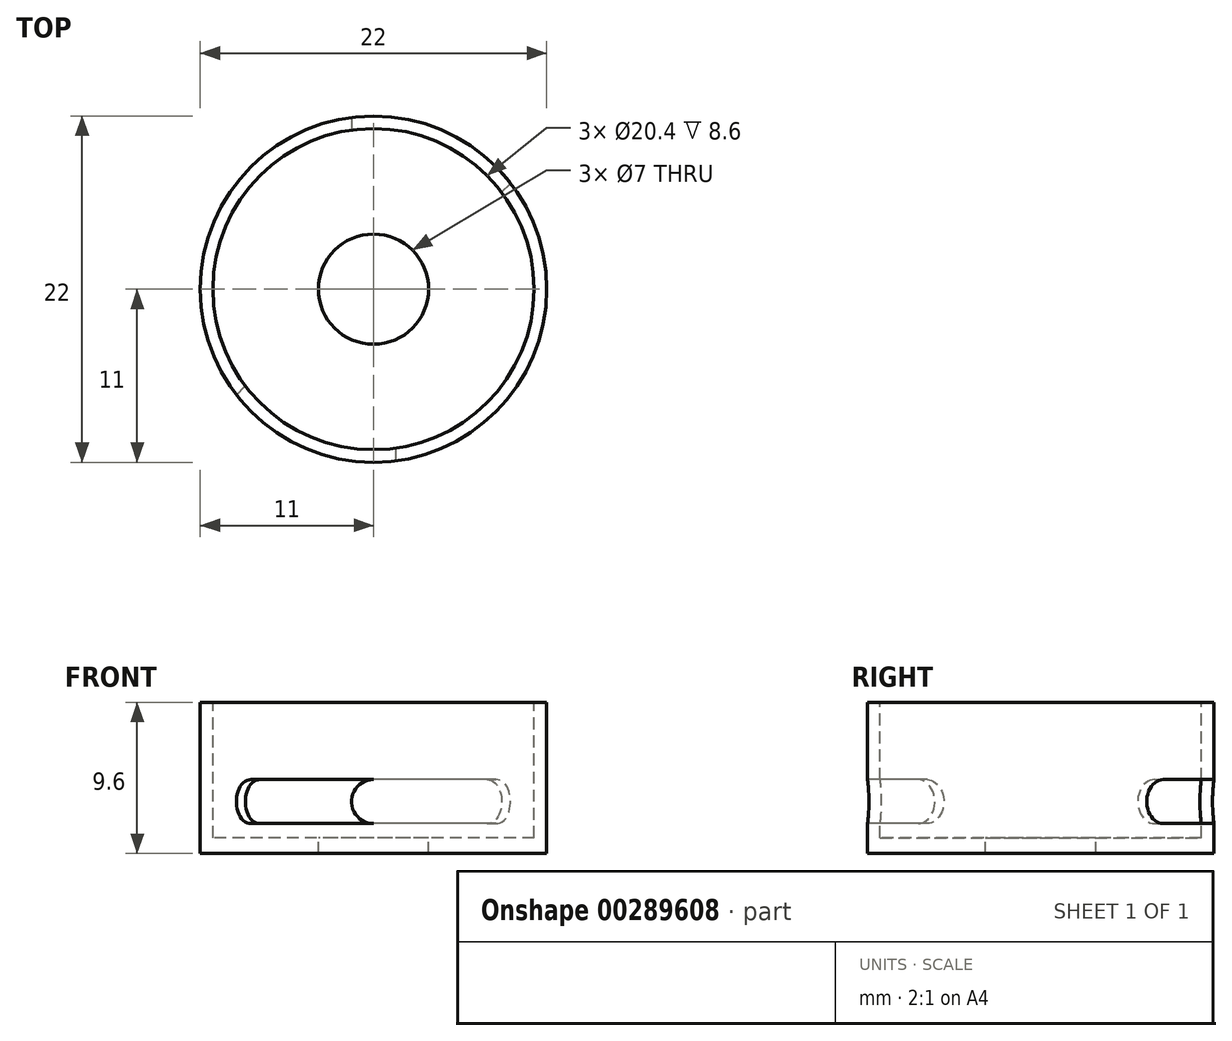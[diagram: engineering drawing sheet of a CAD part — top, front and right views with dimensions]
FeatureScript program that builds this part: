
annotation { "Feature Type Name" : "Feature", "Feature Type Description" : "" }
export const myFeature = defineFeature(function(context is Context, id is Id, definition is map)
    precondition{}
    {
        {
            var Q0;
            Q0=qCreatedBy(makeId("Top.planeOp"),FACE);
            var sketch = newSketch(context, id + "F0", { "sketchPlane" : qUnion([Q0])});
            skCircle(sketch, "E0", {"center": v(0, 0) * mm, "radius": 11 * mm});
            skSolve(sketch);
        }
        {
            var Q0;
            Q0=makeQuery(id+"F0.imprint","IMPRINT",FACE,{"disambiguationData":[TD([[makeQuery(id+"F0.imprint","IMPRINT",EDGE,{"derivedFrom":sQuery(id+"F0.wireOp",EDGE,"E0")}),1.0]])]});
            extrude(context, id + "F1", {"entities" : qUnion([Q0]), "depth" : 9.6 * mm});
        }
        {
            var Q0;
            Q0=makeQuery(id+"F1.opExtrude","CAP_FACE",FACE,{"disambiguationData":[OSD([sQuery(id+"F0.wireOp",EDGE,"E0")])],"isStart":false});
            var sketch = newSketch(context, id + "F2", { "sketchPlane" : qUnion([Q0])});
            skCircle(sketch, "E1", {"center": v(0, 0) * mm, "radius": 10.2 * mm});
            skSolve(sketch);
        }
        {
            var Q0;
            Q0=makeQuery(id+"F2.imprint","IMPRINT",FACE,{"disambiguationData":[TD([[makeQuery(id+"F2.imprint","IMPRINT",EDGE,{"derivedFrom":sQuery(id+"F2.wireOp",EDGE,"E1")}),1.0]])]});
            extrude(context, id + "F3", {"entities" : qUnion([Q0]), "operationType" : NewBodyOperationType.REMOVE, "oppositeDirection" : true, "depth" : 8.6 * mm});
        }
        {
            var Q0;
            Q0=qCreatedBy(makeId("Front.planeOp"),FACE);
            var sketch = newSketch(context, id + "F4", { "sketchPlane" : qUnion([Q0])});
            skCircle(sketch, "E2", {"center": v(0, 3.3) * mm, "radius": 1.4 * mm});
            skSolve(sketch);
        }
        {
            var Q0;
            Q0 = qSketchRegion(id + "F4", true);
            extrude(context, id + "F5", {"entities" : qUnion([Q0]), "operationType" : NewBodyOperationType.REMOVE, "endBound" : BoundingType.SYMMETRIC, "oppositeDirection" : true, "depth" : 25 * mm});
        }
        {
            var Q0;
            Q0=qCreatedBy(makeId("Front.planeOp"),FACE);
            var sketch = newSketch(context, id + "F6", { "sketchPlane" : qUnion([Q0])});
            skLineSegment(sketch, "E3", {"start": v(0, 0) * mm, "end": v(0, 67.55) * mm, "construction": true});
            skSolve(sketch);
        }
        {
            var Q0;
            Q0=sQuery(id+"F6.wireOp",EDGE,"E3");
            cPlane(context, id + "F7", {"entities" : qUnion([Q0]), "cplaneType" : CPlaneType.LINE_ANGLE, "offset" : 25 * mm, "angle" : 45 * degree, "width" : 150 * mm, "height" : 150 * mm});
        }
        {
            var Q0;
            Q0=qCreatedBy(id+"F7.planeOp",FACE);
            var sketch = newSketch(context, id + "F8", { "sketchPlane" : qUnion([Q0])});
            skCircle(sketch, "E4", {"center": v(0, 3.3) * mm, "radius": 1.4 * mm});
            skSolve(sketch);
        }
        {
            var Q0;
            Q0=makeQuery(id+"F8.imprint","IMPRINT",FACE,{"disambiguationData":[TD([[makeQuery(id+"F8.imprint","IMPRINT",EDGE,{"derivedFrom":sQuery(id+"F8.wireOp",EDGE,"E4")}),1.0]])]});
            extrude(context, id + "F9", {"entities" : qUnion([Q0]), "operationType" : NewBodyOperationType.REMOVE, "endBound" : BoundingType.SYMMETRIC, "oppositeDirection" : true, "depth" : 25 * mm});
        }
        {
            var Q0;
            Q0=makeQuery(id+"F3.boolean.opBoolean","COPY",FACE,{"derivedFrom":makeQuery(id+"F3.opExtrude","CAP_FACE",FACE,{"disambiguationData":[OSD([sQuery(id+"F2.wireOp",EDGE,"E1")])],"isStart":false})});
            cPlane(context, id + "F10", {"entities" : qUnion([Q0]), "cplaneType" : CPlaneType.OFFSET, "offset" : 0.9 * mm, "width" : 150 * mm, "height" : 150 * mm});
        }
        {
            var Q0;
            Q0=qCreatedBy(id+"F10.planeOp",FACE);
            var sketch = newSketch(context, id + "F11", { "sketchPlane" : qUnion([Q0])});
            skLineSegment(sketch, "E5", {"start": v(0, 0) * mm, "end": v(0, 13.76) * mm});
            skLineSegment(sketch, "E6", {"start": v(0, 0) * mm, "end": v(9.73, 9.73) * mm});
            skLineSegment(sketch, "E7", {"start": v(9.73, 9.73) * mm, "end": v(0, 13.76) * mm});
            skLineSegment(sketch, "E8", {"start": v(0, 0) * mm, "end": v(0, -13.76) * mm});
            skLineSegment(sketch, "E9", {"start": v(0, 0) * mm, "end": v(-9.73, -9.73) * mm});
            skLineSegment(sketch, "E10", {"start": v(-9.73, -9.73) * mm, "end": v(0, -13.76) * mm});
            skSolve(sketch);
        }
        {
            var Q0;
            Q0=makeQuery(id+"F11.imprint","IMPRINT",FACE,{"disambiguationData":[TD([[makeQuery(id+"F11.imprint","IMPRINT",EDGE,{"derivedFrom":sQuery(id+"F11.wireOp",EDGE,"E5")}),-1.0]])]});
            var Q1;
            Q1=makeQuery(id+"F11.imprint","IMPRINT",FACE,{"disambiguationData":[TD([[makeQuery(id+"F11.imprint","IMPRINT",EDGE,{"derivedFrom":sQuery(id+"F11.wireOp",EDGE,"E8")}),-1.0]])]});
            extrude(context, id + "F12", {"entities" : qUnion([Q0, Q1]), "operationType" : NewBodyOperationType.REMOVE, "depth" : 2.8 * mm});
        }
        {
            var Q0;
            Q0=makeQuery(id+"F3.boolean.opBoolean","COPY",FACE,{"derivedFrom":makeQuery(id+"F3.opExtrude","CAP_FACE",FACE,{"disambiguationData":[OSD([sQuery(id+"F2.wireOp",EDGE,"E1")])],"isStart":false})});
            var sketch = newSketch(context, id + "F13", { "sketchPlane" : qUnion([Q0])});
            skCircle(sketch, "E11", {"center": v(0, 0) * mm, "radius": 3.5 * mm});
            skSolve(sketch);
        }
        {
            var Q0;
            Q0=makeQuery(id+"F13.imprint","IMPRINT",FACE,{"disambiguationData":[TD([[makeQuery(id+"F13.imprint","IMPRINT",EDGE,{"derivedFrom":sQuery(id+"F13.wireOp",EDGE,"E11")}),1.0]])]});
            var Q1;
            Q1=makeQuery(id+"F1.opExtrude","CAP_FACE",FACE,{"disambiguationData":[OSD([sQuery(id+"F0.wireOp",EDGE,"E0")])],"isStart":true});
            extrude(context, id + "F14", {"entities" : qUnion([Q0]), "operationType" : NewBodyOperationType.REMOVE, "endBound" : BoundingType.UP_TO_SURFACE, "oppositeDirection" : true, "endBoundEntityFace" : qUnion([Q1]), "depth" : 25 * mm});
        }
    });
